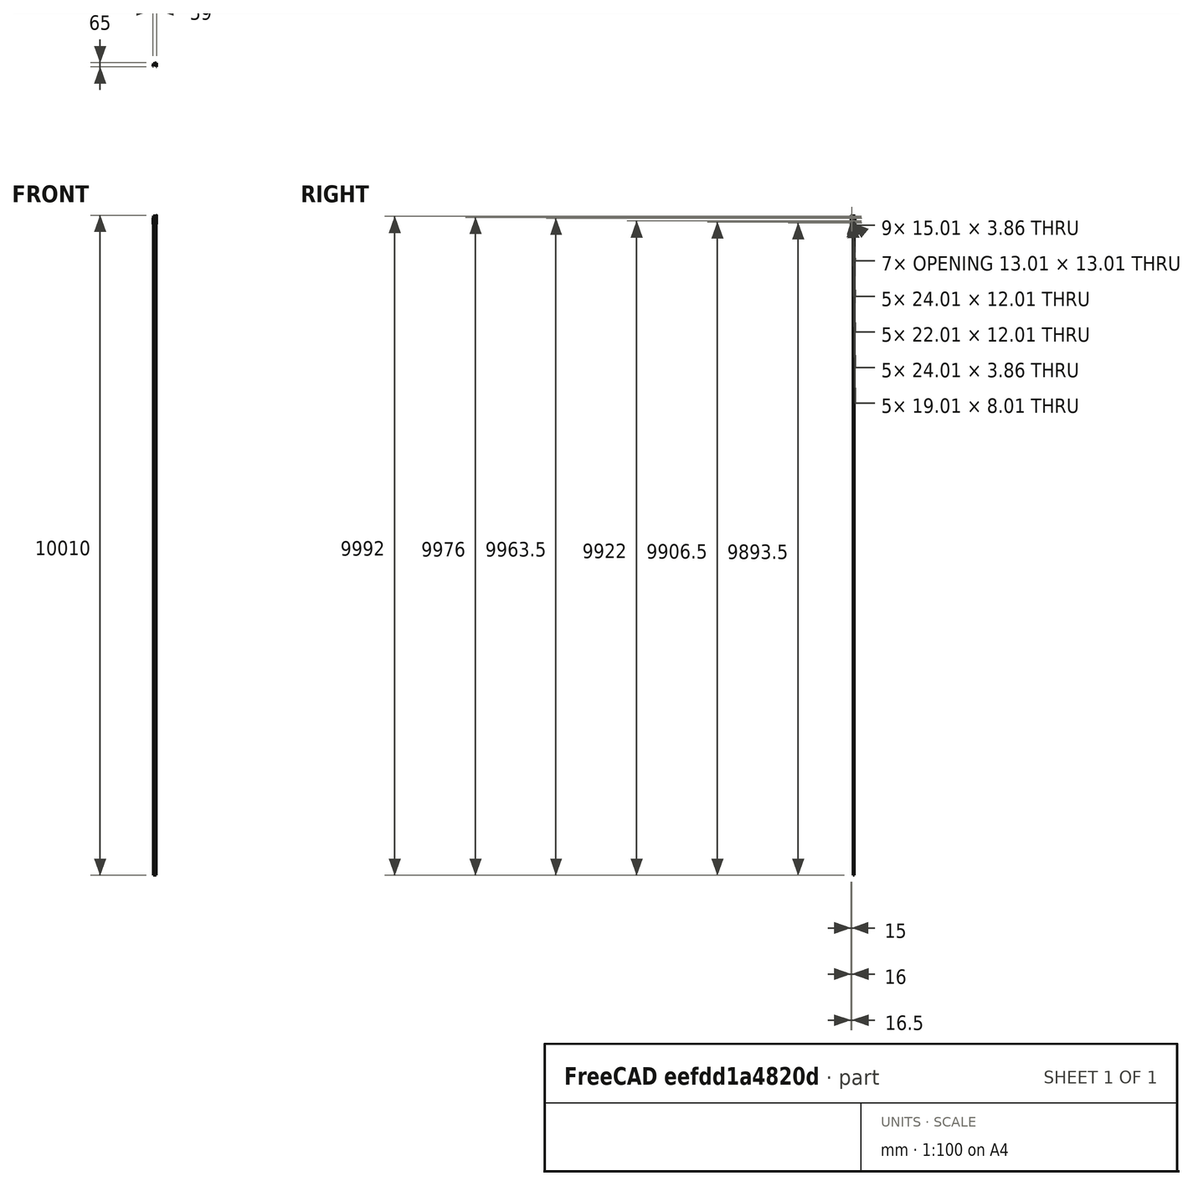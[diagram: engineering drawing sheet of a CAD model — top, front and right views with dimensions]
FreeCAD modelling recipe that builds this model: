
FCSTD DOCUMENT  (FreeCAD 0.16R)
Label: caddy_holder
License: All rights reserved
LicenseURL: http://en.wikipedia.org/wiki/All_rights_reserved
objects: Sketcher::SketchObject×7, PartDesign::Pad×4, Part::Feature×3, PartDesign::Pocket×3, Mesh::Feature×1, PartDesign::Fillet×1
note: 25 computed .brp shape members not serialized (recipe doc carries the construction recipe); baked Part::Feature solids carry a one-line shape summary decoded from their .brp

FEATURE [Mesh::Feature] lulzbot_taz5_tool_caddy_holder_clamp_20
FEATURE [Part::Feature] lulzbot_taz5_tool_caddy_holder_clamp_20001
  shape: bbox 54 x 50 x 125 mm, 1062 faces, 0 solids (baked)
FEATURE [Part::Feature] lulzbot_taz5_tool_caddy_holder_clamp_20001_solid  label="lulzbot_taz5_tool_caddy_holder_clamp_20001 (Solid)"
  shape: bbox 54 x 50 x 125 mm, 1062 faces (baked)
FEATURE [Part::Feature] lulzbot_taz5_tool_caddy_holder_clamp_20001_solid001  label="lulzbot_taz5_tool_caddy_holder_clamp_20001 (Solid)001"
  shape: bbox 54 x 50 x 125 mm, 262 faces (baked)
FEATURE [Sketcher::SketchObject] Sketch
  ExternalGeometry = -> [lulzbot_taz5_tool_caddy_holder_clamp_20001_solid001]
  Placement = pos=(0,0,125) rot=(0,0,1;0rad)
  Support = -> lulzbot_taz5_tool_caddy_holder_clamp_20001_solid001 [Face98]
  sketch-geometry (4):
    g0: LineSegment StartX=-9.86568 StartY=56.8249 StartZ=0 EndX=36.999 EndY=56.8249 EndZ=0
    g1: LineSegment StartX=36.999 StartY=56.8249 StartZ=0 EndX=36.999 EndY=38 EndZ=0
    g2: LineSegment StartX=36.999 StartY=38 StartZ=0 EndX=-9.86568 EndY=38 EndZ=0
    g3: LineSegment StartX=-9.86568 StartY=38 StartZ=0 EndX=-9.86568 EndY=56.8249 EndZ=0
  constraints (9):
    c: Coincident(g0,g1)
    c: Coincident(g1,g2)
    c: Coincident(g2,g3)
    c: Coincident(g3,g0)
    c: Horizontal(g0)
    c: Horizontal(g2)
    c: Vertical(g1)
    c: Vertical(g3)
    c: Coincident(g-3,g1)
FEATURE [PartDesign::Pocket] Pocket
  Length = 5
  Sketch = -> Sketch
  Type = 1
FEATURE [Sketcher::SketchObject] Sketch001
  ExternalGeometry = -> [Pocket]
  Placement = pos=(0,49.001,0) rot=(0,0.707107,0.707107;3.14159rad)
  Support = -> Pocket [Face148]
  sketch-geometry (4):
    g0: LineSegment StartX=-41 StartY=125 StartZ=0 EndX=-36.999 EndY=125 EndZ=0
    g1: LineSegment StartX=-36.999 StartY=125 StartZ=0 EndX=-36.999 EndY=-0.001 EndZ=0
    g2: LineSegment StartX=-36.999 StartY=-0.001 StartZ=0 EndX=-41 EndY=-0.001 EndZ=0
    g3: LineSegment StartX=-41 StartY=-0.001 StartZ=0 EndX=-41 EndY=125 EndZ=0
  constraints (10):
    c: Coincident(g0,g1)
    c: Coincident(g1,g2)
    c: Coincident(g2,g3)
    c: Coincident(g3,g0)
    c: Horizontal(g0)
    c: Horizontal(g2)
    c: Vertical(g1)
    c: Vertical(g3)
    c: Coincident(g1,g-4)
    c: Coincident(g0,g-3)
FEATURE [PartDesign::Pad] Pad
  Length = 10
  Length2 = 100
  Sketch = -> Sketch001
  Type = 0
FEATURE [Sketcher::SketchObject] Sketch002
  ExternalGeometry = -> [Pad]
  Placement = pos=(-10.003,0,0) rot=(0.57735,0.57735,0.57735;2.0944rad)
  Support = -> Pad [Face131]
  sketch-geometry (4):
    g0: LineSegment StartX=12.997 StartY=87.14 StartZ=0 EndX=28.003 EndY=87.14 EndZ=0
    g1: LineSegment StartX=28.003 StartY=87.14 StartZ=0 EndX=28.003 EndY=91.003 EndZ=0
    g2: LineSegment StartX=28.003 StartY=91.003 StartZ=0 EndX=12.997 EndY=91.003 EndZ=0
    g3: LineSegment StartX=12.997 StartY=91.003 StartZ=0 EndX=12.997 EndY=87.14 EndZ=0
  constraints (10):
    c: Coincident(g0,g1)
    c: Coincident(g1,g2)
    c: Coincident(g2,g3)
    c: Coincident(g3,g0)
    c: Horizontal(g0)
    c: Horizontal(g2)
    c: Vertical(g1)
    c: Vertical(g3)
    c: Coincident(g1,g-4)
    c: Coincident(g0,g-3)
FEATURE [PartDesign::Pocket] Pocket001
  Length = 5
  Sketch = -> Sketch002
  Type = 0
FEATURE [Sketcher::SketchObject] Sketch003
  ExternalGeometry = -> [Pocket001]
  Placement = pos=(0,38,0) rot=(0,0.707107,0.707107;3.14159rad)
  Support = -> Pocket001 [Face20]
  sketch-geometry (4):
    g0: LineSegment StartX=-20.999 StartY=0 StartZ=0 EndX=-16.999 EndY=0 EndZ=0
    g1: LineSegment StartX=-16.999 StartY=0 StartZ=0 EndX=-16.999 EndY=125 EndZ=0
    g2: LineSegment StartX=-16.999 StartY=125 StartZ=0 EndX=-20.999 EndY=125 EndZ=0
    g3: LineSegment StartX=-20.999 StartY=125 StartZ=0 EndX=-20.999 EndY=0 EndZ=0
  constraints (12):
    c: Coincident(g0,g1)
    c: Coincident(g1,g2)
    c: Coincident(g2,g3)
    c: Coincident(g3,g0)
    c: Horizontal(g0)
    c: Horizontal(g2)
    c: Vertical(g1)
    c: Vertical(g3)
    c: PointOnObject(g0,g-1)
    c: DistanceX(g-3,g0) = 16
    c: DistanceX(g0,g0) = 4
    c: DistanceY(g2,g-3) = 0
FEATURE [PartDesign::Pad] Pad001
  Length = 30
  Length2 = 100
  Sketch = -> Sketch003
  Type = 0
FEATURE [Sketcher::SketchObject] Sketch004
  ExternalGeometry = -> [Pad001]
  Placement = pos=(-13,0,0) rot=(0.57735,-0.57735,-0.57735;2.0944rad)
  Support = -> Pad001 [Face24]
  sketch-geometry (4):
    g0: LineSegment StartX=-12.003 StartY=86.64 StartZ=0 EndX=-29.003 EndY=86.64 EndZ=0
    g1: LineSegment StartX=-29.003 StartY=86.64 StartZ=0 EndX=-29.003 EndY=91.503 EndZ=0
    g2: LineSegment StartX=-29.003 StartY=91.503 StartZ=0 EndX=-12.003 EndY=91.503 EndZ=0
    g3: LineSegment StartX=-12.003 StartY=91.503 StartZ=0 EndX=-12.003 EndY=86.64 EndZ=0
  constraints (12):
    c: Coincident(g0,g1)
    c: Coincident(g1,g2)
    c: Coincident(g2,g3)
    c: Coincident(g3,g0)
    c: Horizontal(g0)
    c: Horizontal(g2)
    c: Vertical(g1)
    c: Vertical(g3)
    c: DistanceX(g0,g0) = 17
    c: DistanceX(g0,g-4) = 1
    c: DistanceY(g0,g-4) = 0.5
    c: DistanceY(g-4,g2) = 0.5
FEATURE [PartDesign::Pocket] Pocket002
  Length = 5
  Sketch = -> Sketch004
  Type = 0
FEATURE [Sketcher::SketchObject] Sketch005
  ExternalGeometry = -> [Pocket002]
  Placement = pos=(0,0,125) rot=(0,0,1;0rad)
  Support = -> Pocket002 [Face2]
  sketch-geometry (4):
    g0: LineSegment StartX=34 StartY=12.999 StartZ=0 EndX=39 EndY=12.999 EndZ=0
    g1: LineSegment StartX=39 StartY=12.999 StartZ=0 EndX=39 EndY=7.999 EndZ=0
    g2: LineSegment StartX=39 StartY=7.999 StartZ=0 EndX=34 EndY=7.999 EndZ=0
    g3: LineSegment StartX=34 StartY=7.999 StartZ=0 EndX=34 EndY=12.999 EndZ=0
  constraints (12):
    c: Coincident(g0,g1)
    c: Coincident(g1,g2)
    c: Coincident(g2,g3)
    c: Coincident(g3,g0)
    c: Horizontal(g0)
    c: Horizontal(g2)
    c: Vertical(g1)
    c: Vertical(g3)
    c: DistanceY(g-3,g2) = 5
    c: DistanceX(g-3,g2) = 2
    c: DistanceX(g1,g-3) = 2
    c: DistanceY(g1,g1) = 5
FEATURE [PartDesign::Pad] Pad002
  Length = 10
  Length2 = 100
  Sketch = -> Sketch005
  Type = 0
FEATURE [Sketcher::SketchObject] Sketch006
  ExternalGeometry = -> [Pad002]
  Placement = pos=(39,0,0) rot=(0.57735,0.57735,0.57735;2.0944rad)
  Support = -> Pad002 [Face26]
  sketch-geometry (4):
    g0: LineSegment StartX=7.999 StartY=130 StartZ=0 EndX=12.999 EndY=130 EndZ=0
    g1: LineSegment StartX=12.999 StartY=130 StartZ=0 EndX=12.999 EndY=135 EndZ=0
    g2: LineSegment StartX=12.999 StartY=135 StartZ=0 EndX=7.999 EndY=135 EndZ=0
    g3: LineSegment StartX=7.999 StartY=135 StartZ=0 EndX=7.999 EndY=130 EndZ=0
  constraints (11):
    c: Coincident(g0,g1)
    c: Coincident(g1,g2)
    c: Coincident(g2,g3)
    c: Coincident(g3,g0)
    c: Horizontal(g0)
    c: Horizontal(g2)
    c: Vertical(g1)
    c: Vertical(g3)
    c: Coincident(g2,g-3)
    c: Coincident(g1,g-3)
    c: DistanceY(g1,g1) = 5
FEATURE [PartDesign::Pad] Pad003
  Length = 5
  Length2 = 100
  Sketch = -> Sketch006
  Type = 0
FEATURE [PartDesign::Fillet] Fillet
  Base = -> Pad003 [Edge497,Edge376]
  Radius = 2
